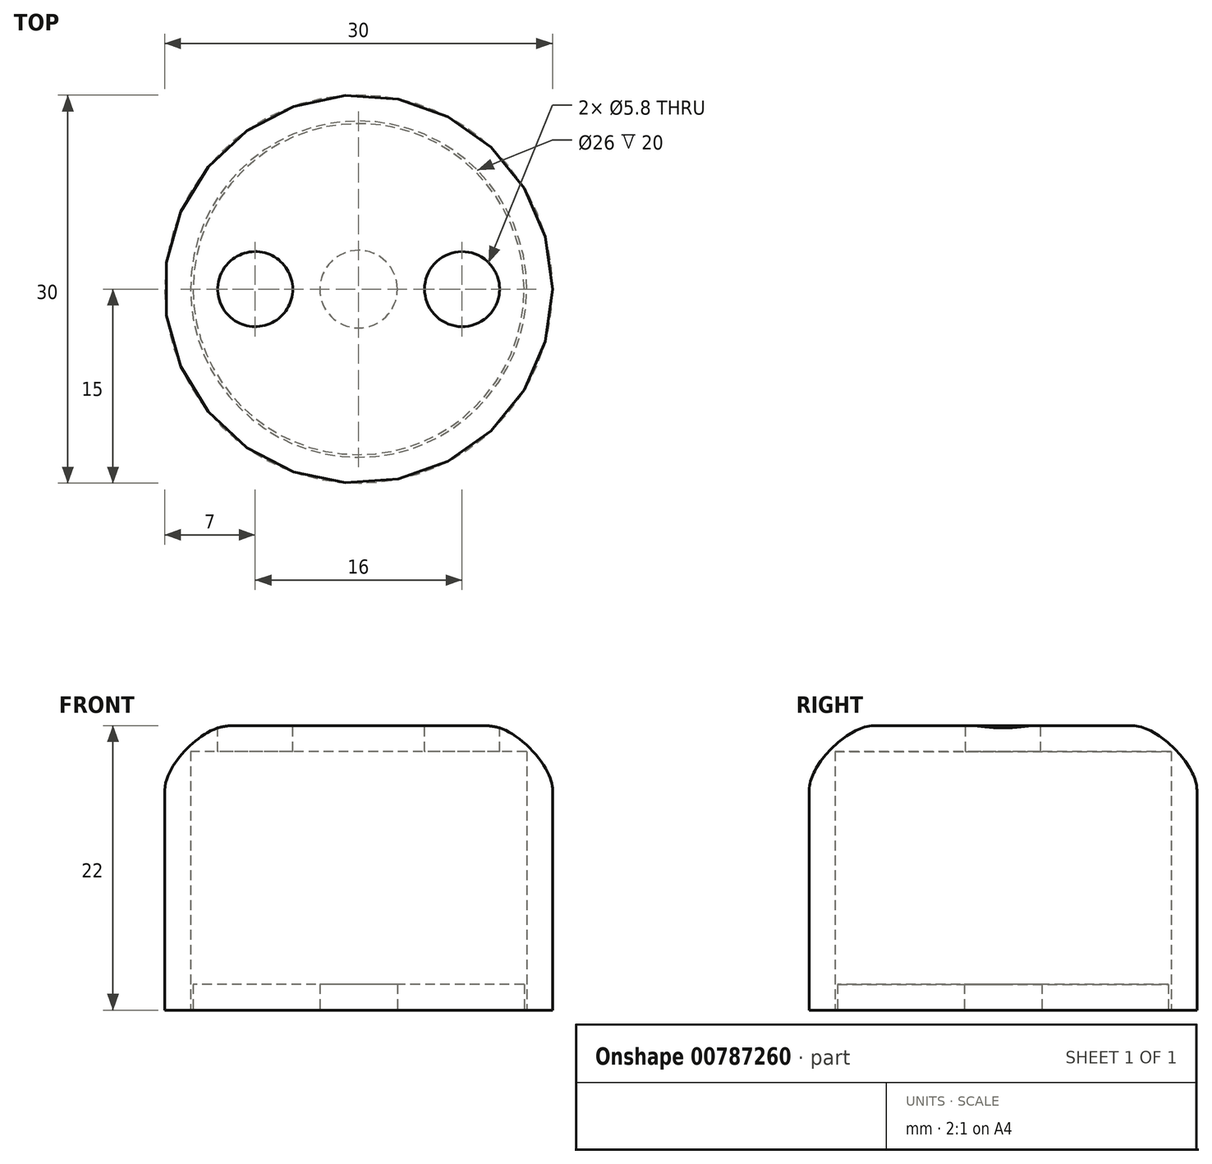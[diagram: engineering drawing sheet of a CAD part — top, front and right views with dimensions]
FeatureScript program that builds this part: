
annotation { "Feature Type Name" : "Feature", "Feature Type Description" : "" }
export const myFeature = defineFeature(function(context is Context, id is Id, definition is map)
    precondition{}
    {
        {
            var Q0;
            Q0=qCreatedBy(makeId("Top.planeOp"),FACE);
            var sketch = newSketch(context, id + "F0", { "sketchPlane" : qUnion([Q0])});
            skCircle(sketch, "E0", {"center": v(0, 0) * mm, "radius": 15 * mm});
            skSolve(sketch);
        }
        {
            var Q0;
            Q0=makeQuery(id+"F0.imprint","IMPRINT",FACE,{"disambiguationData":[TD([[makeQuery(id+"F0.imprint","IMPRINT",EDGE,{"derivedFrom":sQuery(id+"F0.wireOp",EDGE,"E0")}),1.0]])]});
            extrude(context, id + "F1", {"entities" : qUnion([Q0]), "depth" : 22 * mm, "offsetDistance" : 25 * mm});
        }
        {
            var Q0;
            Q0=makeQuery(id+"F1.opExtrude","CAP_EDGE",EDGE,{"disambiguationData":[OSD([sQuery(id+"F0.wireOp",EDGE,"E0")])],"isStart":false});
            fillet(context, id + "F2", {"entities" : qUnion([Q0]), "radius" : 5 * mm, "tangentPropagation" : true, "rho" : 0.3, "crossSection" : FilletCrossSection.CONIC, "allowEdgeOverflow" : false});
        }
        {
            var Q0;
            Q0=makeQuery(id+"F1.opExtrude","CAP_FACE",FACE,{"disambiguationData":[OSD([sQuery(id+"F0.wireOp",EDGE,"E0")])],"isStart":true});
            shell(context, id + "F3", {"entities" : qUnion([Q0]), "thickness" : 2 * mm});
        }
        {
            var Q0;
            Q0=qCreatedBy(makeId("Top.planeOp"),FACE);
            var sketch = newSketch(context, id + "F4", { "sketchPlane" : qUnion([Q0])});
            skCircle(sketch, "E1", {"center": v(0, 0) * mm, "radius": 12.8 * mm});
            skCircle(sketch, "E2", {"center": v(0, 0) * mm, "radius": 3 * mm});
            skSolve(sketch);
        }
        {
            var Q0;
            Q0 = qSketchRegion(id + "F4", true);
            extrude(context, id + "F5", {"entities" : qUnion([Q0]), "depth" : 2 * mm, "offsetDistance" : 25 * mm});
        }
        {
            var Q0;
            Q0=makeQuery(id+"F1.opExtrude","CAP_FACE",FACE,{"disambiguationData":[OSD([sQuery(id+"F0.wireOp",EDGE,"E0")])],"isStart":false});
            var sketch = newSketch(context, id + "F6", { "sketchPlane" : qUnion([Q0])});
            skCircle(sketch, "E3", {"center": v(-8, 0) * mm, "radius": 2.9 * mm});
            skCircle(sketch, "E4", {"center": v(8, 0) * mm, "radius": 2.9 * mm});
            skLineSegment(sketch, "E5", {"start": v(8, 0) * mm, "end": v(0, 0) * mm, "construction": true});
            skLineSegment(sketch, "E6", {"start": v(0, 0) * mm, "end": v(-8, 0) * mm, "construction": true});
            skSolve(sketch);
        }
        {
            var Q0;
            Q0 = qSketchRegion(id + "F6", true);
            extrude(context, id + "F7", {"entities" : qUnion([Q0]), "operationType" : NewBodyOperationType.REMOVE, "oppositeDirection" : true, "depth" : 10 * mm, "offsetDistance" : 25 * mm});
        }
    });
